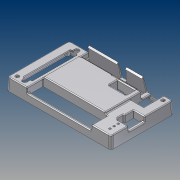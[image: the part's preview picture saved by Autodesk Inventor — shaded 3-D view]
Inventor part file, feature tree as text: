
AUTODESK INVENTOR PART (.ipt)
format: ipt  version: 2012 (Build 160160000, 160)  size: 2,726,912 bytes
history: native  units: mm (DEFAULTED — no unit token found)
features: extrude x22, sketch x13, fillet x7, plane x7, other x6, projected_geometry x1
ambient origin geometry x5: Origin, X Axis, Y Axis, Z Axis, Center Point
bodies: Solid1 (feature_tree)
feature tree (56):
  other  "Basic Profile Sketch"
  extrude  "Above PCB Extrusion"  Depth=71.12mm
  extrude  "Below Extrusion"  Depth=10.16mm
  extrude  "Board Level Edge Cuts"  Depth=2.032mm
  extrude  "Board Level Supports"  Depth=48.1076mm
  extrude  "LED Viewing Angle Increase"  Depth=8.382mm
  other  "DB Sketch"
  extrude  "Side Reliefs"  Depth=4.318mm
  fillet  "Fillet2"  Radius=3.81mm
  extrude  "Board Level Cut"  Depth=25.4mm
  other  "Snap Edge Draft"
  plane  "Work Plane3"
  plane  "Work Plane4"
  plane  "Work Plane5"
  plane  "Work Plane7"
  other  "Snap Sketch"
  extrude  "Relay Snap"  Depth=3.81mm
  extrude  "Relay Snap Cut"  Depth=3.175mm
  extrude  "DIO Snap"  Depth=8.89mm
  extrude  "DIO Snap Cut"  Depth=3.81mm
  extrude  "DIO Snap Cut 2"  Depth=2.032mm
  extrude  "DB Cut"  Depth=3.81mm
  extrude  "Mounting Holes"  Depth=6.35mm
  extrude  "LED, Power, and BFL Holes"  Depth=2.3114mm
  extrude  "I2C Clearance"  Depth=1.27mm
  extrude  "I2C Top Clearance"  Depth=25.4mm
  extrude  "Screw Bosses"  Depth=1.27mm
  other  "Ribs"
  extrude  "Bottom Clearance Cut"  Depth=6.35mm
  other  "Troublesome Components Sketch"
  extrude  "TC Cut 1"  Depth=7.62mm
  extrude  "TC Cut 2"  Depth=35.56mm
  extrude  "TC Cut 3"  Depth=20.32mm
  fillet  "Top Fillets 1"  Radius=5.08mm
  fillet  "Top Fillets 2"  Radius=2.54mm
  fillet  "Rib and Wall Intersection Fillets"  Radius=1.27mm
  fillet  "Bottom Fillets 1"  Radius=25.4mm
  fillet  "Bottom Fillets 2"  Radius=10.16mm
  fillet  "Bottom Fillets 3"  Radius=13.97mm
  plane  "YZ Plane (RIGHT)"
  plane  "XZ Plane (TOP)"
  plane  "XY Plane (FRONT)"
  sketch  "Sketch3"  dims[d0=121.92mm d1=71.12mm]
  sketch  "Sketch9"  dims[d2=2.54mm d3=10.16mm d4=-0.523599mm]
  sketch  "Sketch13"  dims[d5=6.35mm d6=0.523599mm d7=2.032mm]
  sketch  "Sketch14"  dims[d8=10.922mm d9=-0.523599mm]
  sketch  "Sketch15"  dims[d10=14.074mm d11=63.5mm d12=70.844mm d13=5.6261mm d14=63.5mm d15=10.16mm d16=1.016mm d17=1.016mm d18=0.79375mm d19=55.195489mm d20=0.79375mm d21=58.06186mm d22=1.745329mm d24=48.1076mm]
  sketch  "Sketch16"  dims[d27=4.064mm d28=0.523599mm d42=8.382mm d43=-0.523599mm]
  sketch  "Sketch17"  dims[d54=1.22173mm d65=4.318mm d70=3.81mm]
  sketch  "Sketch18"  dims[d71=3.81mm d72=25.4mm d73=0.523599mm]
  sketch  "Sketch20"  dims[d78=3.81mm d79=3.81mm]
  sketch  "Sketch23"  dims[d80=6.35mm d81=3.175mm]
  sketch  "Sketch24"  dims[d82=8.128mm d83=-0.523599mm d84=8.89mm d85=0.349066mm]
  projected_geometry  "Projected Loop2"
  sketch  "Sketch27"  dims[d86=3.81mm d87=3.81mm]
  sketch  "Sketch28"  dims[d88=5.3848mm d89=2.032mm d90=-0.523599mm d94=3.81mm d95=6.35mm d96=2.3114mm d99=1.27mm d100=25.4mm d101=0.174533mm d102=1.27mm d103=2.54mm d104=0.174533mm d105=6.35mm d107=7.62mm d108=35.56mm d109=20.32mm d110=5.08mm d111=2.54mm d112=1.27mm d113=25.4mm d114=10.16mm d116=13.97mm d117=20.32mm d118=2.032mm d119=1.016mm d120=0.762mm d121=2.032mm d123=2.032mm d124=1.016mm d125=1.016mm d126=1.016mm d127=74.93mm d128=15.24mm d129=1.27mm d130=23.495mm d131=1.905mm d132=1.905mm d133=1.016mm d134=5.08mm d135=5.08mm d136=2.54mm d137=6.35mm d138=5.08mm d143=7.62mm d144=0.0mm d146=25.4mm d147=0.0mm d148=0.523599mm d151=25.4mm d152=0.0mm d153=25.4mm d154=0.0mm d155=1.905mm d156=0.523599mm d157=1.27mm d158=7.62mm d159=2.54mm d160=2.54mm d161=2.54mm d162=1.143mm d163=1.016mm d164=0.508mm d166=6.35mm d167=1.27mm d168=0.79375mm d170=45.0deg d172=10.922mm d173=0.762mm d174=38.354mm d175=19.7612mm d176=0.762mm d177=0.762mm d178=5.08mm d179=2.2098mm d180=1.016mm d184=0.762mm d185=2.032mm d186=1.016mm d188=1.396263mm d189=0.872665mm d190=25.4mm d191=0.0mm d194=10.668mm d200=30.0deg d201=1.651mm d202=25.4mm d203=0.0mm d204=18.161mm d206=0.212985mm d208=2.286mm d209=-0.523599mm d213=75.565mm d216=35.56mm d220=1.524mm d221=5.842mm d222=2.54mm d223=2.54mm d224=1.016mm d225=-0.872665mm d226=-0.872665mm d227=-0.872665mm d228=-0.872665mm d231=3.048mm d232=1.016mm d233=1.016mm d237=7.5946mm d238=7.5946mm d239=0.9906mm d240=-0.523599mm d241=20.4724mm d242=4.0132mm d243=4.6482mm d252=23.4442mm d253=4.6736mm d254=16.256mm d255=10.668mm d256=3.6576mm d257=-0.523599mm d258=1.016mm d259=2.032mm d260=0.396875mm d261=0.127mm d262=1.016mm d263=0.396875mm d265=0.508mm d266=0.396875mm d267=0.396875mm d269=14.478mm d270=17.453293mm d271=105.41mm d272=55.88mm d273=26.67mm d274=115.57mm d275=1.524mm d277=47.625mm d278=48.26mm d279=1.143mm d280=5.08mm d281=0.508mm d282=0.508mm d283=7.112mm d284=1.778mm d285=4.8514mm d286=105.41mm d287=0.254mm d288=25.4mm d289=0.523599mm d290=1.016mm d291=1.016mm d292=30.7848mm d293=12.6238mm d294=10.0076mm d295=2.794mm d296=12.7254mm d297=8.2042mm d298=8.0772mm d299=1.524mm d300=1.524mm d301=1.3208mm d302=0.0mm d303=0.254mm d304=1.524mm d305=1.905mm d306=3.048mm d307=1.016mm d308=0.396875mm d309=0.396875mm d310=1.016mm d311=0.508mm d312=0.127mm d313=0.508mm d314=-0.523599mm]
